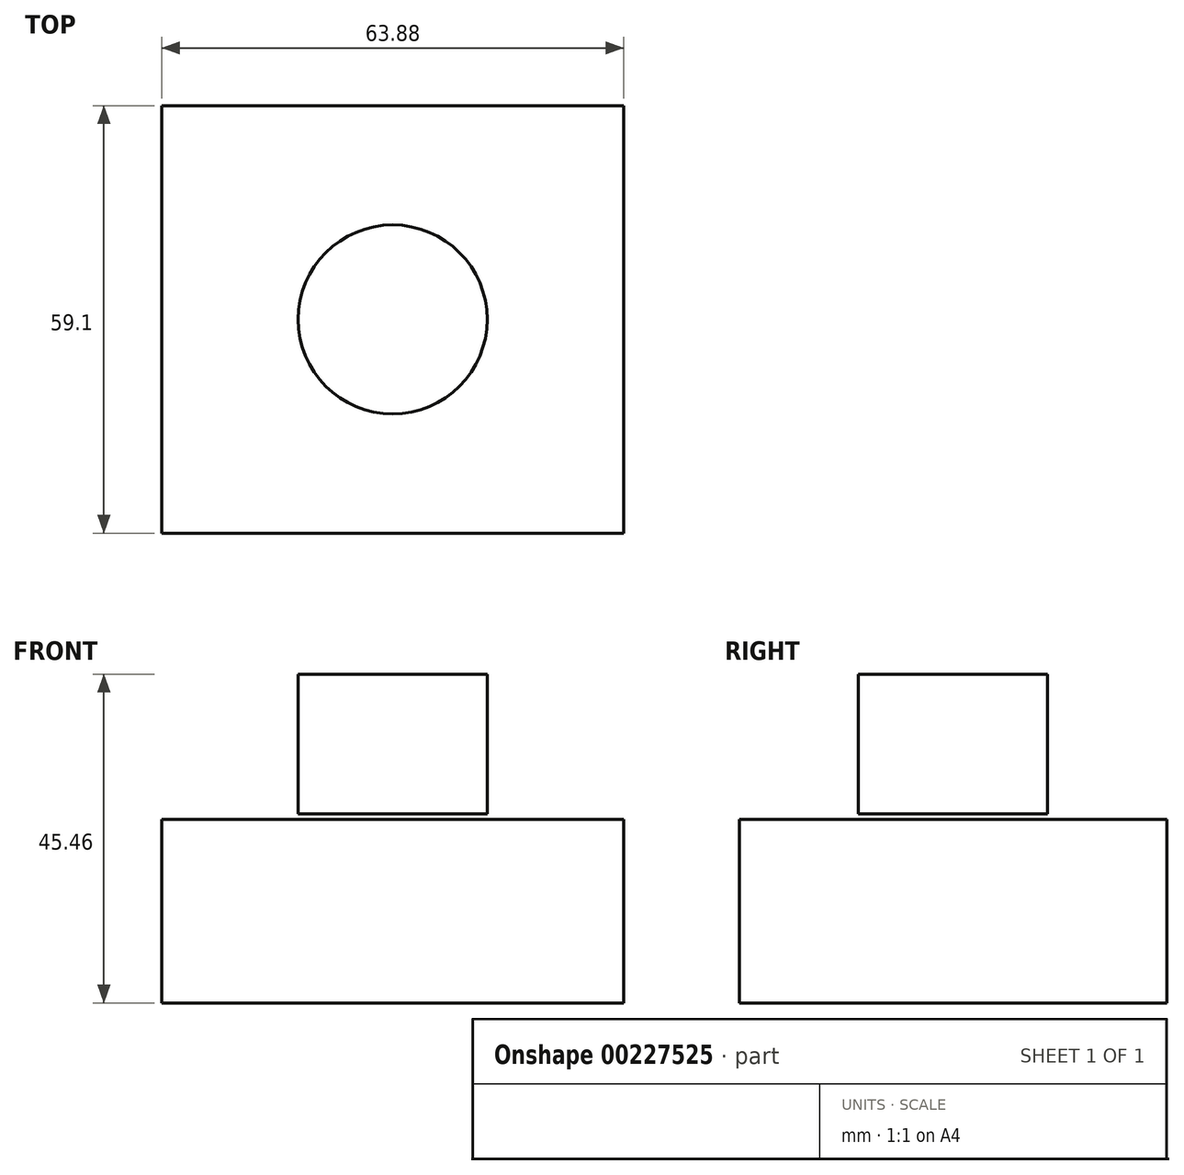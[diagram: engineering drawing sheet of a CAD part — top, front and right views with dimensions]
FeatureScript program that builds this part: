
annotation { "Feature Type Name" : "Feature", "Feature Type Description" : "" }
export const myFeature = defineFeature(function(context is Context, id is Id, definition is map)
    precondition{}
    {
        {
            var Q0;
            Q0=qCreatedBy(makeId("Top.planeOp"),FACE);
            var sketch = newSketch(context, id + "F0", { "sketchPlane" : qUnion([Q0])});
            skLineSegment(sketch, "E0.bottom", {"start": v(31.94, -29.55) * mm, "end": v(-31.94, -29.55) * mm});
            skLineSegment(sketch, "E0.top", {"start": v(31.94, 29.55) * mm, "end": v(-31.94, 29.55) * mm});
            skLineSegment(sketch, "E0.left", {"start": v(31.94, -29.55) * mm, "end": v(31.94, 29.55) * mm});
            skLineSegment(sketch, "E0.right", {"start": v(-31.94, -29.55) * mm, "end": v(-31.94, 29.55) * mm});
            skPoint(sketch, "E0.middle", {"position": v(0, 0) * mm});
            skSolve(sketch);
        }
        {
            var Q0;
            Q0=makeQuery(id+"F0.imprint","IMPRINT",FACE,{"disambiguationData":[TD([[makeQuery(id+"F0.imprint","IMPRINT",EDGE,{"derivedFrom":sQuery(id+"F0.wireOp",EDGE,"E0.bottom")}),-1.0]])]});
            extrude(context, id + "F1", {"entities" : qUnion([Q0]), "depth" : 25.4 * mm});
        }
        {
            var Q0;
            Q0=qCreatedBy(makeId("Right.planeOp"),FACE);
            var sketch = newSketch(context, id + "F2", { "sketchPlane" : qUnion([Q0])});
            skLineSegment(sketch, "E1.bottom", {"start": v(0, 45.46) * mm, "end": v(13.07, 45.46) * mm});
            skLineSegment(sketch, "E1.top", {"start": v(0, 26.14) * mm, "end": v(13.07, 26.14) * mm});
            skLineSegment(sketch, "E1.left", {"start": v(0, 45.46) * mm, "end": v(0, 26.14) * mm});
            skLineSegment(sketch, "E1.right", {"start": v(13.07, 45.46) * mm, "end": v(13.07, 26.14) * mm});
            skSolve(sketch);
        }
        {
            var Q0;
            Q0=makeQuery(id+"F2.imprint","IMPRINT",FACE,{"disambiguationData":[TD([[makeQuery(id+"F2.imprint","IMPRINT",EDGE,{"derivedFrom":sQuery(id+"F2.wireOp",EDGE,"E1.bottom")}),-1.0]])]});
            var Q1;
            Q1=sQuery(id+"F2.wireOp",EDGE,"E1.left");
            revolve(context, id + "F3", {"entities" : qUnion([Q0]), "axis" : qUnion([Q1]), "revolveType" : RevolveType.FULL});
        }
    });
